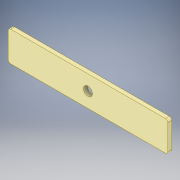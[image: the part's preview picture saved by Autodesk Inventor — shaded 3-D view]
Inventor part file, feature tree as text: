
AUTODESK INVENTOR PART (.ipt)
format: ipt  version: 2017 (Build 210142000, 142)  size: 102,912 bytes
history: native  units: in
note: dims shown in document units (in); Inventor stores cm internally (conversion verified against a paired STEP export)
features: extrude x1, fillet x1, sketch x1
ambient origin geometry x8: Origin, YZ Plane, XZ Plane, XY Plane, X Axis, Y Axis, Z Axis, Center Point
bodies: Solid1 (feature_tree)
feature tree (3):
  extrude  "Extrusion1"  Depth=1.5in
  fillet  "Fillet1"  Radius=0.45in
  sketch  "Sketch1"  dims[d0=8.0in d1=1.5in d2=0.45in d3=0.2in d4=0.0in d5=0.125in]
